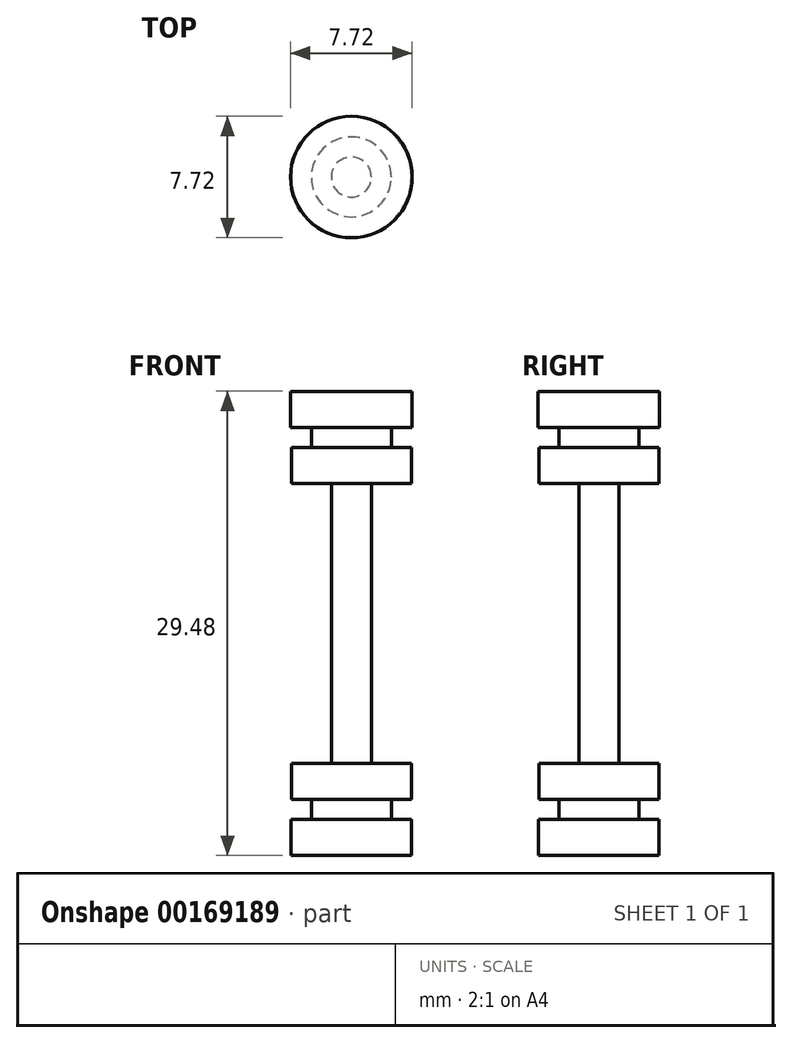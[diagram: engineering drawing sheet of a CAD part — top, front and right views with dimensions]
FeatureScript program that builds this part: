
annotation { "Feature Type Name" : "Feature", "Feature Type Description" : "" }
export const myFeature = defineFeature(function(context is Context, id is Id, definition is map)
    precondition{}
    {
        {
            var Q0;
            Q0=qCreatedBy(makeId("Front.planeOp"),FACE);
            var sketch = newSketch(context, id + "F0", { "sketchPlane" : qUnion([Q0])});
            skLineSegment(sketch, "E0.bottom", {"start": v(-1.27, 8.9) * mm, "end": v(1.27, 8.9) * mm});
            skLineSegment(sketch, "E0.top", {"start": v(-1.27, -8.9) * mm, "end": v(1.27, -8.9) * mm});
            skLineSegment(sketch, "E0.left", {"start": v(-1.27, 8.9) * mm, "end": v(-1.27, -8.9) * mm});
            skLineSegment(sketch, "E0.right", {"start": v(1.27, 8.9) * mm, "end": v(1.27, -8.9) * mm});
            skPoint(sketch, "E0.middle", {"position": v(0, 0) * mm});
            skLineSegment(sketch, "E1.bottom", {"start": v(-3.8, 8.9) * mm, "end": v(3.81, 8.9) * mm});
            skLineSegment(sketch, "E1.top", {"start": v(-3.8, 11.18) * mm, "end": v(3.81, 11.18) * mm});
            skLineSegment(sketch, "E1.left", {"start": v(-3.8, 8.9) * mm, "end": v(-3.8, 11.18) * mm});
            skLineSegment(sketch, "E1.right", {"start": v(3.81, 8.9) * mm, "end": v(3.81, 11.18) * mm});
            skPoint(sketch, "E1.middle", {"position": v(0, 10.04) * mm});
            skLineSegment(sketch, "E2.bottom", {"start": v(-3.81, -8.9) * mm, "end": v(3.8, -8.9) * mm});
            skLineSegment(sketch, "E2.top", {"start": v(-3.81, -11.18) * mm, "end": v(3.8, -11.18) * mm});
            skLineSegment(sketch, "E2.left", {"start": v(-3.81, -8.9) * mm, "end": v(-3.81, -11.18) * mm});
            skLineSegment(sketch, "E2.right", {"start": v(3.8, -8.9) * mm, "end": v(3.8, -11.18) * mm});
            skPoint(sketch, "E2.middle", {"position": v(0, -10.04) * mm});
            skLineSegment(sketch, "E3.bottom", {"start": v(-2.54, 11.18) * mm, "end": v(2.54, 11.18) * mm});
            skLineSegment(sketch, "E3.top", {"start": v(-2.54, 12.45) * mm, "end": v(2.54, 12.45) * mm});
            skLineSegment(sketch, "E3.left", {"start": v(-2.54, 11.18) * mm, "end": v(-2.54, 12.45) * mm});
            skLineSegment(sketch, "E3.right", {"start": v(2.54, 11.18) * mm, "end": v(2.54, 12.45) * mm});
            skPoint(sketch, "E3.middle", {"position": v(0, 11.81) * mm});
            skLineSegment(sketch, "E4.bottom", {"start": v(-2.54, -11.18) * mm, "end": v(2.54, -11.18) * mm});
            skLineSegment(sketch, "E4.top", {"start": v(-2.54, -12.45) * mm, "end": v(2.54, -12.45) * mm});
            skLineSegment(sketch, "E4.left", {"start": v(-2.54, -11.18) * mm, "end": v(-2.54, -12.45) * mm});
            skLineSegment(sketch, "E4.right", {"start": v(2.54, -11.18) * mm, "end": v(2.54, -12.45) * mm});
            skPoint(sketch, "E4.middle", {"position": v(0, -11.82) * mm});
            skLineSegment(sketch, "E5.bottom", {"start": v(-3.86, 12.45) * mm, "end": v(3.86, 12.45) * mm});
            skLineSegment(sketch, "E5.top", {"start": v(-3.86, 14.74) * mm, "end": v(3.86, 14.74) * mm});
            skLineSegment(sketch, "E5.left", {"start": v(-3.86, 12.45) * mm, "end": v(-3.86, 14.74) * mm});
            skLineSegment(sketch, "E5.right", {"start": v(3.86, 12.45) * mm, "end": v(3.86, 14.74) * mm});
            skPoint(sketch, "E5.middle", {"position": v(0, 13.6) * mm});
            skLineSegment(sketch, "E6.bottom", {"start": v(-3.83, -12.45) * mm, "end": v(3.83, -12.45) * mm});
            skLineSegment(sketch, "E6.top", {"start": v(-3.83, -14.74) * mm, "end": v(3.83, -14.74) * mm});
            skLineSegment(sketch, "E6.left", {"start": v(-3.83, -12.45) * mm, "end": v(-3.83, -14.74) * mm});
            skLineSegment(sketch, "E6.right", {"start": v(3.83, -12.45) * mm, "end": v(3.83, -14.74) * mm});
            skPoint(sketch, "E6.middle", {"position": v(0, -13.6) * mm});
            skPoint(sketch, "E6.middle.positionSnap0", {"position": v(0, -12.45) * mm});
            skPoint(sketch, "E6.centerSnap0", {"position": v(0, -12.45) * mm});
            skLineSegment(sketch, "E7", {"start": v(0, 14.74) * mm, "end": v(0, -16.7) * mm});
            skPoint(sketch, "E7.endSnap0", {"position": v(0, -14.74) * mm});
            skSolve(sketch);
        }
        {
            var Q0;
            {var subQ0=sQuery(id+"F0.wireOp",EDGE,"E5.left");Q0=makeQuery(id+"F0.imprint","IMPRINT",FACE,{"disambiguationData":[TD([[makeQuery(id+"F0.imprint","IMPRINT",EDGE,{"derivedFrom":subQ0}),-1.0]])]});}
            var Q1;
            {var subQ0=sQuery(id+"F0.wireOp",EDGE,"E3.left");Q1=makeQuery(id+"F0.imprint","IMPRINT",FACE,{"disambiguationData":[TD([[makeQuery(id+"F0.imprint","IMPRINT",EDGE,{"derivedFrom":subQ0}),-1.0]])]});}
            var Q2;
            {var subQ5=sQuery(id+"F0.wireOp",EDGE,"E1.left");Q2=makeQuery(id+"F0.imprint","IMPRINT",FACE,{"disambiguationData":[TD([[makeQuery(id+"F0.imprint","IMPRINT",EDGE,{"derivedFrom":subQ5}),-1.0]])]});}
            var Q3;
            {var subQ0=sQuery(id+"F0.wireOp",EDGE,"E0.left");Q3=makeQuery(id+"F0.imprint","IMPRINT",FACE,{"disambiguationData":[TD([[makeQuery(id+"F0.imprint","IMPRINT",EDGE,{"derivedFrom":subQ0}),1.0]])]});}
            var Q4;
            {var subQ5=sQuery(id+"F0.wireOp",EDGE,"E2.left");Q4=makeQuery(id+"F0.imprint","IMPRINT",FACE,{"disambiguationData":[TD([[makeQuery(id+"F0.imprint","IMPRINT",EDGE,{"derivedFrom":subQ5}),1.0]])]});}
            var Q5;
            {var subQ0=sQuery(id+"F0.wireOp",EDGE,"E4.left");Q5=makeQuery(id+"F0.imprint","IMPRINT",FACE,{"disambiguationData":[TD([[makeQuery(id+"F0.imprint","IMPRINT",EDGE,{"derivedFrom":subQ0}),1.0]])]});}
            var Q6;
            {var subQ0=sQuery(id+"F0.wireOp",EDGE,"E6.left");Q6=makeQuery(id+"F0.imprint","IMPRINT",FACE,{"disambiguationData":[TD([[makeQuery(id+"F0.imprint","IMPRINT",EDGE,{"derivedFrom":subQ0}),1.0]])]});}
            var Q7;
            Q7=sQuery(id+"F0.wireOp",EDGE,"E7");
            revolve(context, id + "F1", {"entities" : qUnion([Q0, Q1, Q2, Q3, Q4, Q5, Q6]), "axis" : qUnion([Q7]), "revolveType" : RevolveType.FULL});
        }
    });
